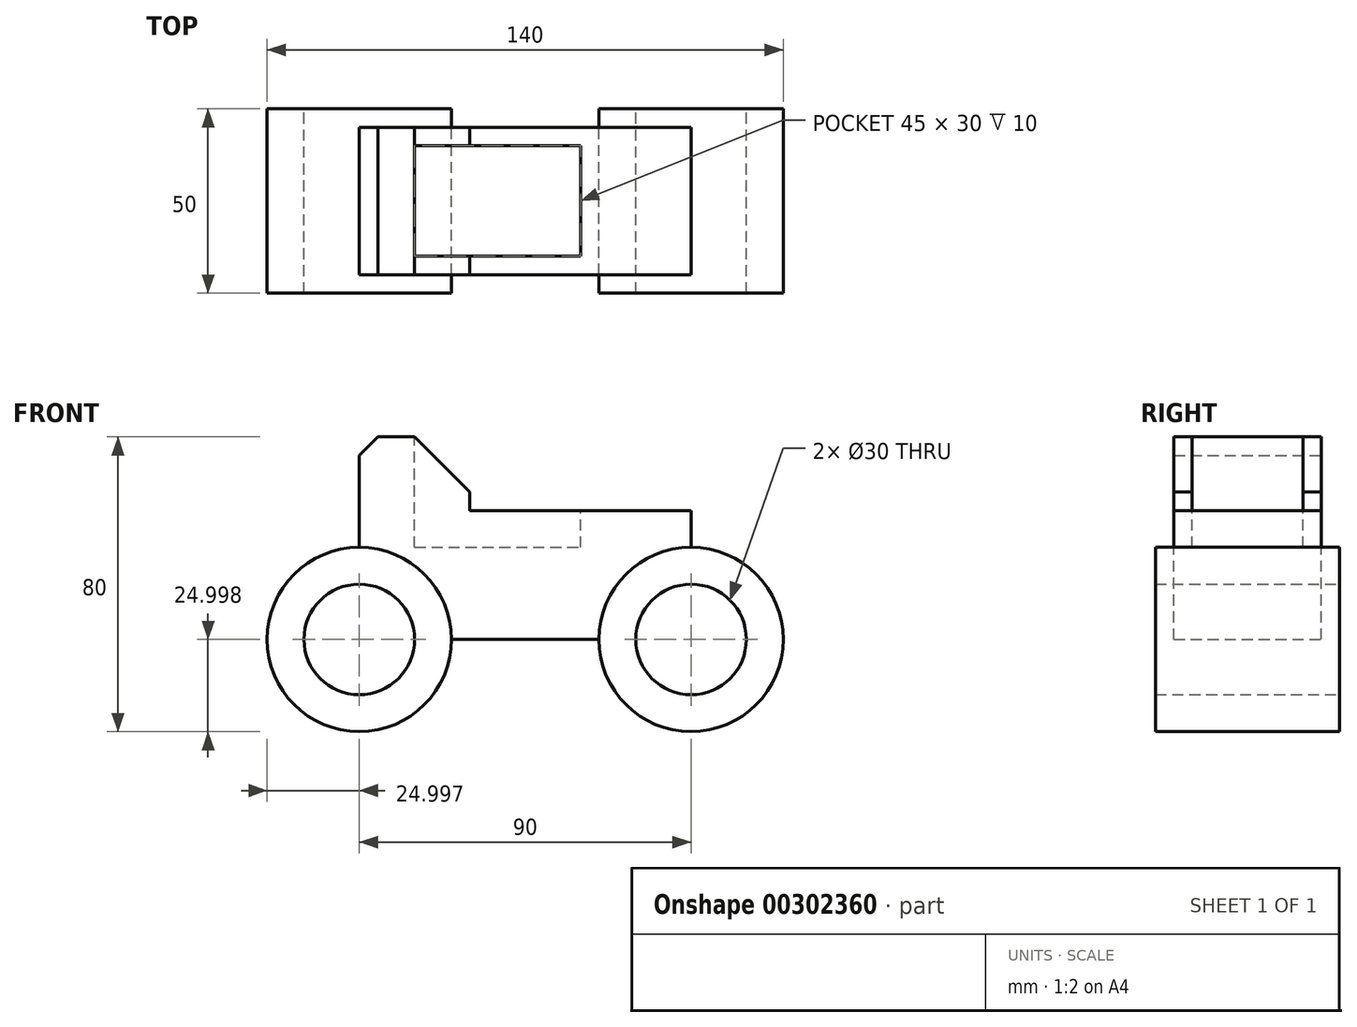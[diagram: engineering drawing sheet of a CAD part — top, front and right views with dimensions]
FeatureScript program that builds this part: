
annotation { "Feature Type Name" : "Feature", "Feature Type Description" : "" }
export const myFeature = defineFeature(function(context is Context, id is Id, definition is map)
    precondition{}
    {
        {
            var Q0;
            Q0=qCreatedBy(makeId("Front.planeOp"),FACE);
            var sketch = newSketch(context, id + "F0", { "sketchPlane" : qUnion([Q0])});
            skLineSegment(sketch, "E0.bottom", {"start": v(-49.21, 22.49) * mm, "end": v(40.79, 22.49) * mm});
            skLineSegment(sketch, "E0.top", {"start": v(-49.21, -32.51) * mm, "end": v(40.79, -32.51) * mm});
            skLineSegment(sketch, "E0.left", {"start": v(-49.21, 22.49) * mm, "end": v(-49.21, -32.51) * mm});
            skLineSegment(sketch, "E0.right", {"start": v(40.79, 22.49) * mm, "end": v(40.79, -32.51) * mm});
            skCircle(sketch, "E1", {"center": v(-49.21, -32.51) * mm, "radius": 25 * mm});
            skCircle(sketch, "E2", {"center": v(40.79, -32.51) * mm, "radius": 25 * mm});
            skCircle(sketch, "E3", {"center": v(-49.21, -32.51) * mm, "radius": 15 * mm});
            skCircle(sketch, "E4", {"center": v(40.79, -32.51) * mm, "radius": 15 * mm});
            skLineSegment(sketch, "E5", {"start": v(-44.21, 22.49) * mm, "end": v(-49.21, 17.49) * mm});
            skLineSegment(sketch, "E6", {"start": v(-34.21, 22.49) * mm, "end": v(-19.21, 7.49) * mm});
            skLineSegment(sketch, "E7", {"start": v(-19.21, 7.49) * mm, "end": v(-19.21, 2.49) * mm});
            skLineSegment(sketch, "E8", {"start": v(-19.21, 2.49) * mm, "end": v(40.79, 2.49) * mm});
            skSolve(sketch);
        }
        {
            var Q0;
            {var subQ4=sQuery(id+"F0.wireOp",EDGE,"E5");Q0=makeQuery(id+"F0.imprint","IMPRINT",FACE,{"disambiguationData":[TD([[makeQuery(id+"F0.imprint","IMPRINT",EDGE,{"derivedFrom":subQ4}),1.0]])]});}
            var Q1;
            {var subQ0=sQuery(id+"F0.wireOp",EDGE,"E1");var subQ1=sQuery(id+"F0.wireOp",EDGE,"E0.top");var subQ2=makeQuery(id+"F0.imprint","INTERSECT",VERTEX,{"derivedFrom":[subQ1,subQ0]});Q1=makeQuery(id+"F0.imprint","IMPRINT",FACE,{"disambiguationData":[TD([[makeQuery(id+"F0.imprint","IMPRINT",EDGE,{"disambiguationData":[TD([[subQ2,1.0]])],"derivedFrom":subQ1}),-1.0]])]});}
            var Q2;
            {var subQ0=sQuery(id+"F0.wireOp",EDGE,"E1");var subQ1=sQuery(id+"F0.wireOp",EDGE,"E0.top");var subQ2=makeQuery(id+"F0.imprint","INTERSECT",VERTEX,{"derivedFrom":[subQ1,subQ0]});Q2=makeQuery(id+"F0.imprint","IMPRINT",FACE,{"disambiguationData":[TD([[makeQuery(id+"F0.imprint","IMPRINT",EDGE,{"disambiguationData":[TD([[subQ2,1.0]])],"derivedFrom":subQ1}),1.0]])]});}
            var Q3;
            {var subQ0=sQuery(id+"F0.wireOp",EDGE,"E2");var subQ1=sQuery(id+"F0.wireOp",EDGE,"E0.top");var subQ2=makeQuery(id+"F0.imprint","INTERSECT",VERTEX,{"derivedFrom":[subQ1,subQ0]});Q3=makeQuery(id+"F0.imprint","IMPRINT",FACE,{"disambiguationData":[TD([[makeQuery(id+"F0.imprint","IMPRINT",EDGE,{"disambiguationData":[TD([[subQ2,-1.0]])],"derivedFrom":subQ1}),1.0]])]});}
            var Q4;
            {var subQ0=sQuery(id+"F0.wireOp",EDGE,"E2");var subQ1=sQuery(id+"F0.wireOp",EDGE,"E0.top");var subQ2=makeQuery(id+"F0.imprint","INTERSECT",VERTEX,{"derivedFrom":[subQ1,subQ0]});Q4=makeQuery(id+"F0.imprint","IMPRINT",FACE,{"disambiguationData":[TD([[makeQuery(id+"F0.imprint","IMPRINT",EDGE,{"disambiguationData":[TD([[subQ2,-1.0]])],"derivedFrom":subQ1}),-1.0]])]});}
            extrude(context, id + "F1", {"entities" : qUnion([Q0, Q1, Q2, Q3, Q4]), "depth" : 50 * mm});
        }
        {
            var Q0;
            {var subQ4=sQuery(id+"F0.wireOp",EDGE,"E5");Q0=makeQuery(id+"F0.imprint","IMPRINT",FACE,{"disambiguationData":[TD([[makeQuery(id+"F0.imprint","IMPRINT",EDGE,{"derivedFrom":subQ4}),1.0]])]});}
            extrude(context, id + "F2", {"entities" : qUnion([Q0]), "operationType" : NewBodyOperationType.REMOVE, "depth" : 5 * mm});
        }
        {
            var Q0;
            Q0=makeQuery(id+"F1.opExtrude","CAP_FACE",FACE,{"disambiguationData":[OSD([sQuery(id+"F0.wireOp",EDGE,"E0.bottom"),sQuery(id+"F0.wireOp",EDGE,"E0.top"),sQuery(id+"F0.wireOp",EDGE,"E0.left"),sQuery(id+"F0.wireOp",EDGE,"E0.right"),sQuery(id+"F0.wireOp",EDGE,"E1"),sQuery(id+"F0.wireOp",EDGE,"E2"),sQuery(id+"F0.wireOp",EDGE,"E3"),sQuery(id+"F0.wireOp",EDGE,"E4"),sQuery(id+"F0.wireOp",EDGE,"E5"),sQuery(id+"F0.wireOp",EDGE,"E6"),sQuery(id+"F0.wireOp",EDGE,"E7"),sQuery(id+"F0.wireOp",EDGE,"E8")])],"isStart":false});
            var sketch = newSketch(context, id + "F3", { "sketchPlane" : qUnion([Q0])});
            skLineSegment(sketch, "E9.bottom", {"start": v(-49.21, 22.49) * mm, "end": v(40.79, 22.49) * mm});
            skLineSegment(sketch, "E9.top", {"start": v(-49.21, -32.51) * mm, "end": v(40.79, -32.51) * mm});
            skLineSegment(sketch, "E9.left", {"start": v(-49.21, 22.49) * mm, "end": v(-49.21, -32.51) * mm});
            skLineSegment(sketch, "E9.right", {"start": v(40.79, 22.49) * mm, "end": v(40.79, -32.51) * mm});
            skCircle(sketch, "E10", {"center": v(-49.21, -32.51) * mm, "radius": 25 * mm});
            skCircle(sketch, "E11", {"center": v(40.79, -32.51) * mm, "radius": 25 * mm});
            skSolve(sketch);
        }
        {
            var Q0;
            {var subQ5=makeQuery(id+"F1.opExtrude","CAP_EDGE",EDGE,{"disambiguationData":[OSD([sQuery(id+"F0.wireOp",EDGE,"E5")])],"isStart":false});Q0=makeQuery(id+"F3.imprint","IMPRINT",FACE,{"disambiguationData":[TD([[makeQuery(id+"F3.imprint","IMPRINT",EDGE,{"derivedFrom":subQ5}),1.0]])]});}
            extrude(context, id + "F4", {"entities" : qUnion([Q0]), "operationType" : NewBodyOperationType.REMOVE, "oppositeDirection" : true, "depth" : 5 * mm});
        }
        {
            var Q0;
            Q0=makeQuery(id+"F1.opExtrude","SWEPT_FACE",FACE,{"disambiguationData":[OSD([sQuery(id+"F0.wireOp",EDGE,"E8")])]});
            var sketch = newSketch(context, id + "F5", { "sketchPlane" : qUnion([Q0])});
            skLineSegment(sketch, "E12.bottom", {"start": v(-19.21, -10) * mm, "end": v(10.79, -10) * mm});
            skLineSegment(sketch, "E12.top", {"start": v(-19.21, -40) * mm, "end": v(10.79, -40) * mm});
            skLineSegment(sketch, "E12.left", {"start": v(-19.21, -10) * mm, "end": v(-19.21, -40) * mm});
            skLineSegment(sketch, "E12.right", {"start": v(10.79, -10) * mm, "end": v(10.79, -40) * mm});
            skSolve(sketch);
        }
        {
            var Q0;
            Q0=makeQuery(id+"F5.imprint","IMPRINT",FACE,{"disambiguationData":[TD([[makeQuery(id+"F5.imprint","IMPRINT",EDGE,{"derivedFrom":sQuery(id+"F5.wireOp",EDGE,"E12.bottom")}),-1.0]])]});
            extrude(context, id + "F6", {"entities" : qUnion([Q0]), "operationType" : NewBodyOperationType.REMOVE, "oppositeDirection" : true, "depth" : 10 * mm});
        }
        {
            var Q0;
            Q0=makeQuery(id+"F6.boolean.opBoolean","MERGE",FACE,{"derivedFrom":[makeQuery(id+"F1.opExtrude","SWEPT_FACE",FACE,{"disambiguationData":[OSD([sQuery(id+"F0.wireOp",EDGE,"E7")])]}),makeQuery(id+"F6.opExtrude","SWEPT_FACE",FACE,{"disambiguationData":[OSD([sQuery(id+"F5.wireOp",EDGE,"E12.left")])]})]});
            var sketch = newSketch(context, id + "F7", { "sketchPlane" : qUnion([Q0])});
            skLineSegment(sketch, "E13.bottom", {"start": v(-40, -7.51) * mm, "end": v(-10, -7.51) * mm});
            skLineSegment(sketch, "E13.top", {"start": v(-40, 27.63) * mm, "end": v(-10, 27.63) * mm});
            skLineSegment(sketch, "E13.left", {"start": v(-40, -7.51) * mm, "end": v(-40, 27.63) * mm});
            skLineSegment(sketch, "E13.right", {"start": v(-10, -7.51) * mm, "end": v(-10, 27.63) * mm});
            skSolve(sketch);
        }
        {
            var Q0;
            {var subQ10=sQuery(id+"F7.wireOp",EDGE,"E13.bottom");Q0=makeQuery(id+"F7.imprint","IMPRINT",FACE,{"disambiguationData":[TD([[makeQuery(id+"F7.imprint","IMPRINT",EDGE,{"derivedFrom":subQ10}),1.0]])]});}
            var Q1;
            {var subQ0=sQuery(id+"F7.wireOp",EDGE,"E13.top");Q1=makeQuery(id+"F7.imprint","IMPRINT",FACE,{"disambiguationData":[TD([[makeQuery(id+"F7.imprint","IMPRINT",EDGE,{"derivedFrom":subQ0}),-1.0]])]});}
            extrude(context, id + "F8", {"entities" : qUnion([Q0, Q1]), "operationType" : NewBodyOperationType.REMOVE, "oppositeDirection" : true, "depth" : 15 * mm});
        }
    });
